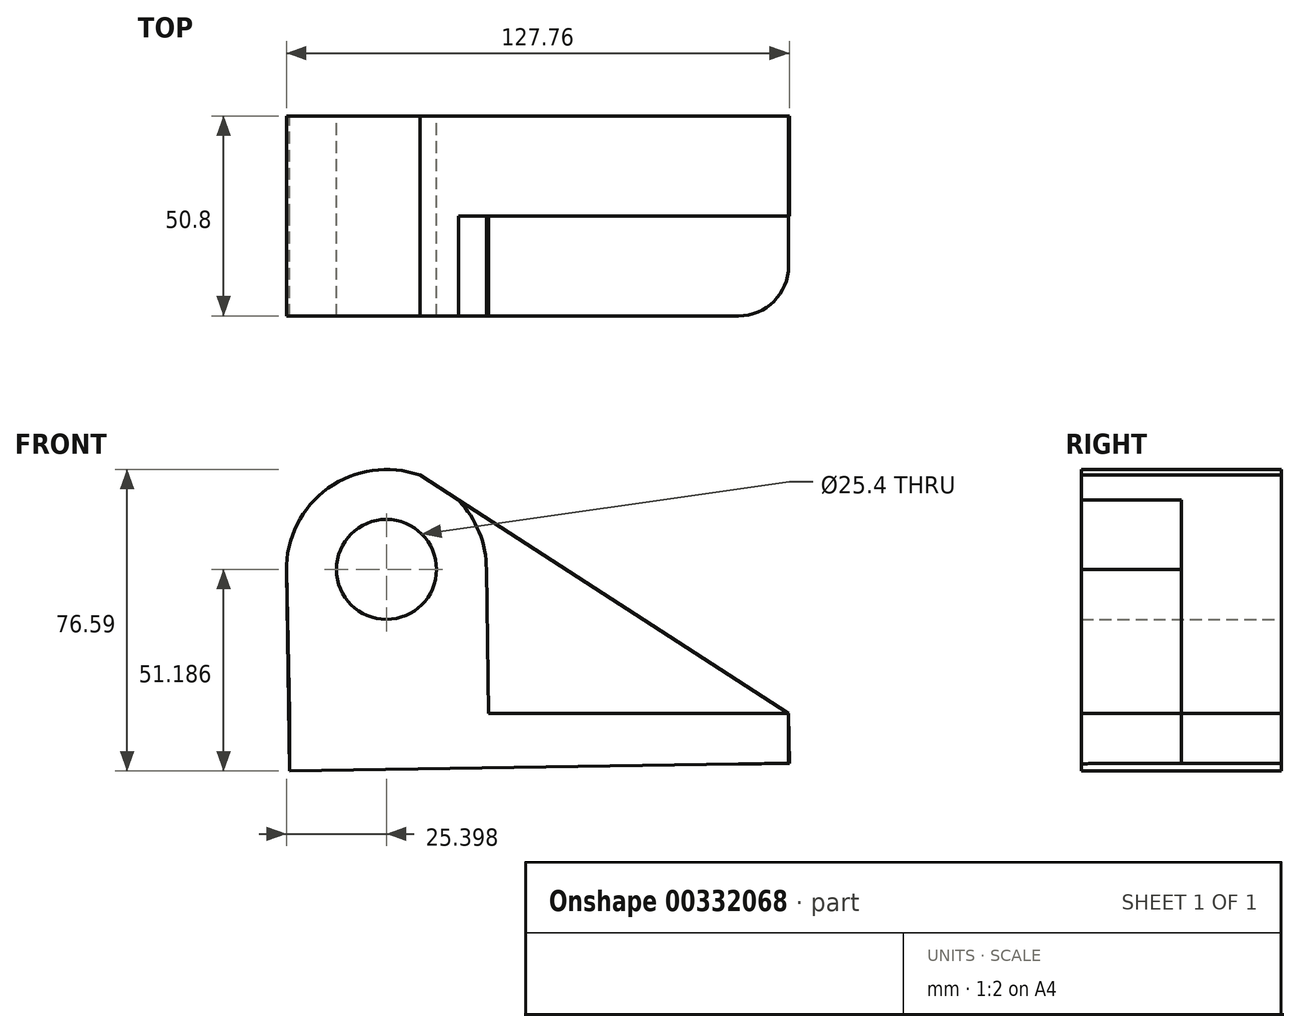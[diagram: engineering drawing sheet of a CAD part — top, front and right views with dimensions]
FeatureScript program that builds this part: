
annotation { "Feature Type Name" : "Feature", "Feature Type Description" : "" }
export const myFeature = defineFeature(function(context is Context, id is Id, definition is map)
    precondition{}
    {
        {
            var Q0;
            Q0=qCreatedBy(makeId("Front.planeOp"),FACE);
            var sketch = newSketch(context, id + "F0", { "sketchPlane" : qUnion([Q0])});
            skCircle(sketch, "E0", {"center": v(-79.55, -13.8) * mm, "radius": 12.7 * mm});
            skArc(sketch, "E1", {"start": v(-61.23, 3.8) * mm, "mid": v(-89.21, 9.7) * mm, "end": v(-104.95, -14.18) * mm});
            skLineSegment(sketch, "E2.bottom", {"start": v(-216.9, 14.73) * mm, "end": v(-213.43, 14.73) * mm});
            skLineSegment(sketch, "E2.top", {"start": v(-216.9, -4.33) * mm, "end": v(-213.43, -4.33) * mm});
            skLineSegment(sketch, "E3", {"start": v(-104.95, -14.18) * mm, "end": v(-104.18, -64.98) * mm});
            skLineSegment(sketch, "E4", {"start": v(22.8, -63.04) * mm, "end": v(22.62, -50.34) * mm});
            skLineSegment(sketch, "E5", {"start": v(22.62, -50.34) * mm, "end": v(-71.05, 10.14) * mm});
            skLineSegment(sketch, "E6", {"start": v(-104.18, -64.98) * mm, "end": v(22.8, -63.04) * mm});
            skSolve(sketch);
        }
        {
            var Q0;
            Q0=makeQuery(id+"F0.imprint","IMPRINT",FACE,{"disambiguationData":[TD([[makeQuery(id+"F0.imprint","IMPRINT",EDGE,{"derivedFrom":sQuery(id+"F0.wireOp",EDGE,"E0")}),-1.0]])]});
            extrude(context, id + "F1", {"entities" : qUnion([Q0]), "depth" : 25.4 * mm});
        }
        {
            var Q0;
            Q0=makeQuery(id+"F1.opExtrude","CAP_FACE",FACE,{"disambiguationData":[OSD([sQuery(id+"F0.wireOp",EDGE,"E0"),sQuery(id+"F0.wireOp",EDGE,"E1"),sQuery(id+"F0.wireOp",EDGE,"E3"),sQuery(id+"F0.wireOp",EDGE,"E4"),sQuery(id+"F0.wireOp",EDGE,"E5"),sQuery(id+"F0.wireOp",EDGE,"E6")])],"isStart":false});
            var sketch = newSketch(context, id + "F2", { "sketchPlane" : qUnion([Q0])});
            skCircle(sketch, "E7", {"center": v(-79.55, -13.8) * mm, "radius": 12.7 * mm});
            skArc(sketch, "E8", {"start": v(-54.15, -13.8) * mm, "mid": v(-79.9, 11.6) * mm, "end": v(-104.94, -14.5) * mm});
            skLineSegment(sketch, "E9.bottom", {"start": v(22.62, -50.34) * mm, "end": v(-53.6, -50.34) * mm});
            skLineSegment(sketch, "E9.top", {"start": v(22.62, -64.98) * mm, "end": v(-104.18, -64.98) * mm});
            skLineSegment(sketch, "E9.left", {"start": v(22.62, -50.34) * mm, "end": v(22.62, -64.98) * mm});
            skLineSegment(sketch, "E9.right", {"start": v(-104.18, -50.34) * mm, "end": v(-104.18, -64.98) * mm});
            skLineSegment(sketch, "E10", {"start": v(-54.15, -13.8) * mm, "end": v(-53.6, -50.34) * mm});
            skPoint(sketch, "E10.endSnap0", {"position": v(-104.18, -57.66) * mm});
            skLineSegment(sketch, "E11", {"start": v(-104.95, -14.18) * mm, "end": v(-104.18, -50.34) * mm});
            skPoint(sketch, "E12.orphan", {"position": v(-53.48, -57.66) * mm});
            skSolve(sketch);
        }
        {
            var Q0;
            Q0=makeQuery(id+"F2.imprint","IMPRINT",FACE,{"disambiguationData":[TD([[makeQuery(id+"F2.imprint","IMPRINT",EDGE,{"derivedFrom":sQuery(id+"F2.wireOp",EDGE,"E7")}),-1.0]])]});
            extrude(context, id + "F3", {"entities" : qUnion([Q0]), "operationType" : NewBodyOperationType.ADD, "depth" : 25.4 * mm});
        }
        {
            var Q0;
            Q0=makeQuery(id+"F3.opExtrude","CAP_EDGE",EDGE,{"disambiguationData":[OSD([sQuery(id+"F2.wireOp",EDGE,"E9.left")])],"isStart":false});
            fillet(context, id + "F4", {"entities" : qUnion([Q0]), "radius" : 12.7 * mm, "tangentPropagation" : true, "allowEdgeOverflow" : false});
        }
    });
